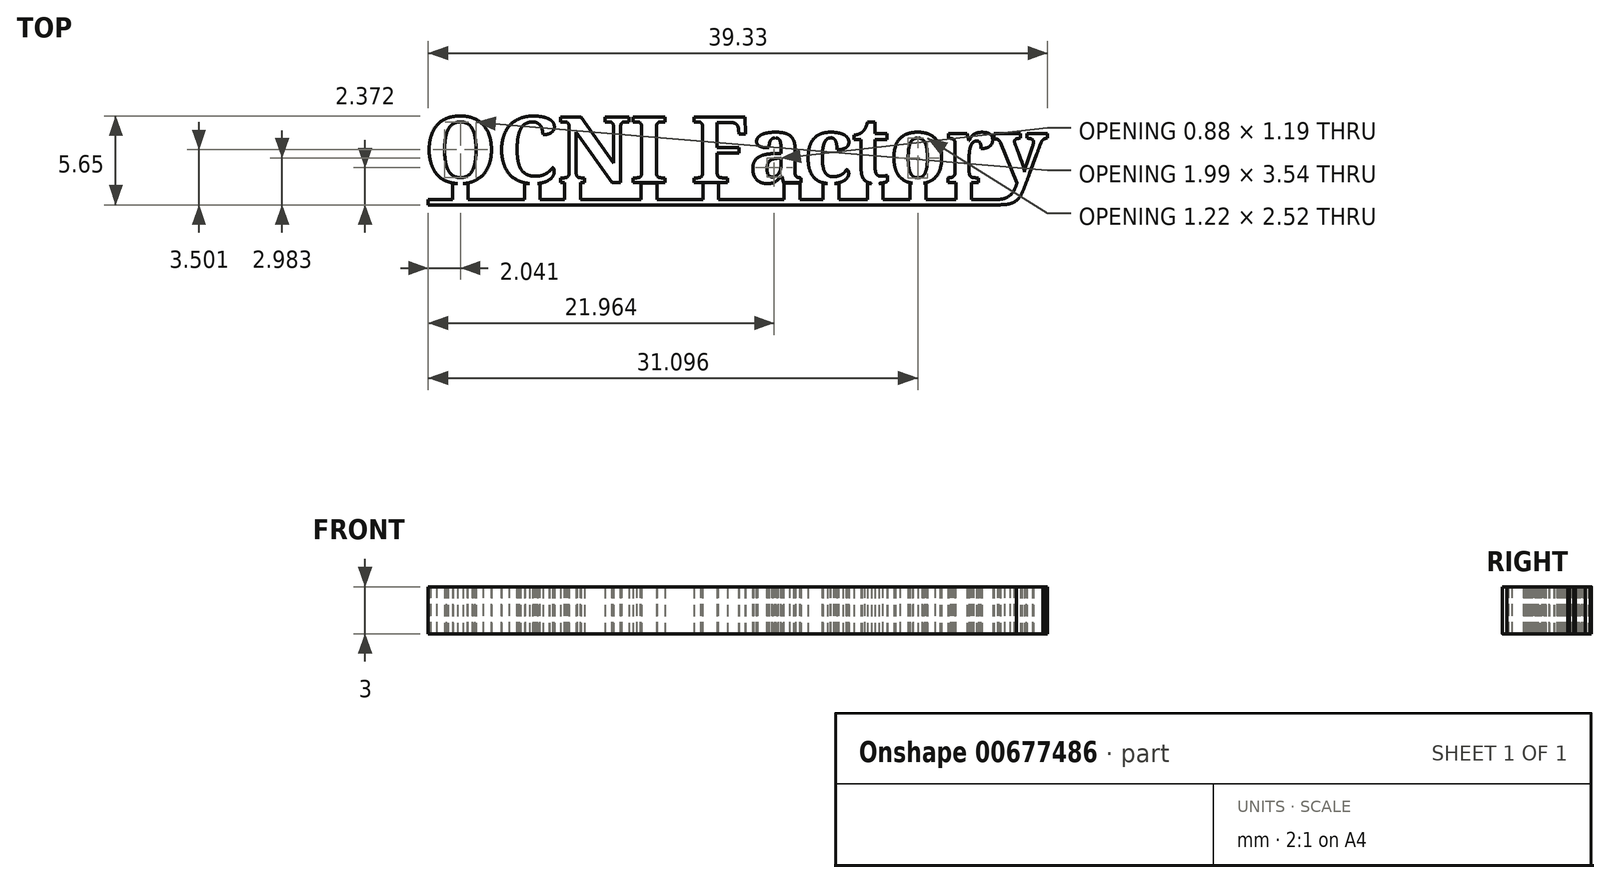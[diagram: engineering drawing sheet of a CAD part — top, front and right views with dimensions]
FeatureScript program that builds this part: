
annotation { "Feature Type Name" : "Feature", "Feature Type Description" : "" }
export const myFeature = defineFeature(function(context is Context, id is Id, definition is map)
    precondition{}
    {
        {
            var Q0;
            Q0=qCreatedBy(makeId("Top.planeOp"),FACE);
            var sketch = newSketch(context, id + "F0", { "sketchPlane" : qUnion([Q0])});
            skText(sketch, "E0", { "text": "OCNI Factory", "fontName": "NotoSerif-Bold.ttf"});
            const initialGuessF0  = {"E0": [-0.00492, -0.00147, 1, 0, 0.00421]};
            skSetInitialGuess(sketch, initialGuessF0);
            skSolve(sketch);
        }
        {
            var Q0;
            Q0 = qSketchRegion(id + "F0", true);
            extrude(context, id + "F1", {"entities" : qUnion([Q0]), "depth" : 3 * mm, "offsetDistance" : 25 * mm});
        }
        {
            var Q0;
            Q0=makeQuery(id+"F1.opExtrude","SWEPT_FACE",FACE,{"disambiguationData":[OSD([sQuery(id+"F0.wireOp",EDGE,"E0.sketch_text.stroke-369")])]});
            var Q1;
            Q1=makeQuery(id+"F1.opExtrude","SWEPT_FACE",FACE,{"disambiguationData":[OSD([sQuery(id+"F0.wireOp",EDGE,"E0.sketch_text.stroke-8")])]});
            extrude(context, id + "F2", {"entities" : qUnion([Q0]), "operationType" : NewBodyOperationType.ADD, "depth" : 36.1 * mm, "endBoundEntityFace" : qUnion([Q1]), "offsetDistance" : 25 * mm});
        }
        {
            var Q0;
            Q0=qCreatedBy(makeId("Top.planeOp"),FACE);
            var sketch = newSketch(context, id + "F3", { "sketchPlane" : qUnion([Q0])});
            skLineSegment(sketch, "E1.bottom", {"start": v(-3.12, -1.52) * mm, "end": v(-2.12, -1.52) * mm});
            skLineSegment(sketch, "E1.top", {"start": v(-3.12, -2.87) * mm, "end": v(-2.12, -2.87) * mm});
            skLineSegment(sketch, "E1.left", {"start": v(-3.12, -1.52) * mm, "end": v(-3.12, -2.87) * mm});
            skLineSegment(sketch, "E1.right", {"start": v(-2.12, -1.52) * mm, "end": v(-2.12, -2.87) * mm});
            skLineSegment(sketch, "E2.bottom", {"start": v(1.46, -1.52) * mm, "end": v(2.46, -1.52) * mm});
            skLineSegment(sketch, "E2.top", {"start": v(1.46, -2.87) * mm, "end": v(2.46, -2.87) * mm});
            skLineSegment(sketch, "E2.left", {"start": v(1.46, -1.52) * mm, "end": v(1.46, -2.87) * mm});
            skLineSegment(sketch, "E2.right", {"start": v(2.46, -1.52) * mm, "end": v(2.46, -2.87) * mm});
            skLineSegment(sketch, "E3.bottom", {"start": v(4, -1.44) * mm, "end": v(5, -1.44) * mm});
            skLineSegment(sketch, "E3.top", {"start": v(4, -2.8) * mm, "end": v(5, -2.8) * mm});
            skLineSegment(sketch, "E3.left", {"start": v(4, -1.44) * mm, "end": v(4, -2.8) * mm});
            skLineSegment(sketch, "E3.right", {"start": v(5, -1.44) * mm, "end": v(5, -2.8) * mm});
            skLineSegment(sketch, "E4.bottom", {"start": v(8.87, -1.47) * mm, "end": v(9.87, -1.47) * mm});
            skLineSegment(sketch, "E4.top", {"start": v(8.87, -2.83) * mm, "end": v(9.87, -2.83) * mm});
            skLineSegment(sketch, "E4.left", {"start": v(8.87, -1.47) * mm, "end": v(8.87, -2.83) * mm});
            skLineSegment(sketch, "E4.right", {"start": v(9.87, -1.47) * mm, "end": v(9.87, -2.83) * mm});
            skLineSegment(sketch, "E5.bottom", {"start": v(12.79, -1.47) * mm, "end": v(13.79, -1.47) * mm});
            skLineSegment(sketch, "E5.top", {"start": v(12.79, -2.85) * mm, "end": v(13.79, -2.85) * mm});
            skLineSegment(sketch, "E5.left", {"start": v(12.79, -1.47) * mm, "end": v(12.79, -2.85) * mm});
            skLineSegment(sketch, "E5.right", {"start": v(13.79, -1.47) * mm, "end": v(13.79, -2.85) * mm});
            skLineSegment(sketch, "E6.bottom", {"start": v(17.95, -1.48) * mm, "end": v(18.95, -1.48) * mm});
            skLineSegment(sketch, "E6.top", {"start": v(17.95, -2.84) * mm, "end": v(18.95, -2.84) * mm});
            skLineSegment(sketch, "E6.left", {"start": v(17.95, -1.48) * mm, "end": v(17.95, -2.84) * mm});
            skLineSegment(sketch, "E6.right", {"start": v(18.95, -1.48) * mm, "end": v(18.95, -2.84) * mm});
            skLineSegment(sketch, "E7.bottom", {"start": v(20.43, -1.52) * mm, "end": v(21.43, -1.52) * mm});
            skLineSegment(sketch, "E7.top", {"start": v(20.43, -2.87) * mm, "end": v(21.43, -2.87) * mm});
            skLineSegment(sketch, "E7.left", {"start": v(20.43, -1.52) * mm, "end": v(20.43, -2.87) * mm});
            skLineSegment(sketch, "E7.right", {"start": v(21.43, -1.52) * mm, "end": v(21.43, -2.87) * mm});
            skLineSegment(sketch, "E8.bottom", {"start": v(23.23, -1.51) * mm, "end": v(24.23, -1.51) * mm});
            skLineSegment(sketch, "E8.top", {"start": v(23.23, -2.87) * mm, "end": v(24.23, -2.87) * mm});
            skLineSegment(sketch, "E8.left", {"start": v(23.23, -1.51) * mm, "end": v(23.23, -2.87) * mm});
            skLineSegment(sketch, "E8.right", {"start": v(24.23, -1.51) * mm, "end": v(24.23, -2.87) * mm});
            skLineSegment(sketch, "E9.bottom", {"start": v(25.94, -1.5) * mm, "end": v(26.94, -1.5) * mm});
            skLineSegment(sketch, "E9.top", {"start": v(25.94, -2.85) * mm, "end": v(26.94, -2.85) * mm});
            skLineSegment(sketch, "E9.left", {"start": v(25.94, -1.5) * mm, "end": v(25.94, -2.85) * mm});
            skLineSegment(sketch, "E9.right", {"start": v(26.94, -1.5) * mm, "end": v(26.94, -2.85) * mm});
            skLineSegment(sketch, "E10.bottom", {"start": v(28.85, -1.46) * mm, "end": v(29.85, -1.46) * mm});
            skLineSegment(sketch, "E10.top", {"start": v(28.85, -2.8) * mm, "end": v(29.85, -2.8) * mm});
            skLineSegment(sketch, "E10.left", {"start": v(28.85, -1.46) * mm, "end": v(28.85, -2.8) * mm});
            skLineSegment(sketch, "E10.right", {"start": v(29.85, -1.46) * mm, "end": v(29.85, -2.8) * mm});
            skSolve(sketch);
        }
        {
            var Q0;
            Q0 = qSketchRegion(id + "F3", true);
            var Q1;
            {var subQ0=sQuery(id+"F0.wireOp",EDGE,"E0.sketch_text.stroke-369");Q1=makeQuery(id+"F2.boolean.opBoolean","MERGE",FACE,{"derivedFrom":[makeQuery(id+"F1.opExtrude","CAP_FACE",FACE,{"disambiguationData":[OSD([sQuery(id+"F0.wireOp",EDGE,"E0.sketch_text.stroke-353"),sQuery(id+"F0.wireOp",EDGE,"E0.sketch_text.stroke-354"),sQuery(id+"F0.wireOp",EDGE,"E0.sketch_text.stroke-355"),sQuery(id+"F0.wireOp",EDGE,"E0.sketch_text.stroke-356"),sQuery(id+"F0.wireOp",EDGE,"E0.sketch_text.stroke-357"),sQuery(id+"F0.wireOp",EDGE,"E0.sketch_text.stroke-358"),sQuery(id+"F0.wireOp",EDGE,"E0.sketch_text.stroke-359"),sQuery(id+"F0.wireOp",EDGE,"E0.sketch_text.stroke-360"),sQuery(id+"F0.wireOp",EDGE,"E0.sketch_text.stroke-361"),sQuery(id+"F0.wireOp",EDGE,"E0.sketch_text.stroke-362"),sQuery(id+"F0.wireOp",EDGE,"E0.sketch_text.stroke-363"),sQuery(id+"F0.wireOp",EDGE,"E0.sketch_text.stroke-364"),sQuery(id+"F0.wireOp",EDGE,"E0.sketch_text.stroke-365"),sQuery(id+"F0.wireOp",EDGE,"E0.sketch_text.stroke-366"),sQuery(id+"F0.wireOp",EDGE,"E0.sketch_text.stroke-367"),sQuery(id+"F0.wireOp",EDGE,"E0.sketch_text.stroke-368"),subQ0,sQuery(id+"F0.wireOp",EDGE,"E0.sketch_text.stroke-370"),sQuery(id+"F0.wireOp",EDGE,"E0.sketch_text.stroke-371"),sQuery(id+"F0.wireOp",EDGE,"E0.sketch_text.stroke-372"),sQuery(id+"F0.wireOp",EDGE,"E0.sketch_text.stroke-373"),sQuery(id+"F0.wireOp",EDGE,"E0.sketch_text.stroke-374"),sQuery(id+"F0.wireOp",EDGE,"E0.sketch_text.stroke-375"),sQuery(id+"F0.wireOp",EDGE,"E0.sketch_text.stroke-376"),sQuery(id+"F0.wireOp",EDGE,"E0.sketch_text.stroke-377"),sQuery(id+"F0.wireOp",EDGE,"E0.sketch_text.stroke-378"),sQuery(id+"F0.wireOp",EDGE,"E0.sketch_text.stroke-379"),sQuery(id+"F0.wireOp",EDGE,"E0.sketch_text.stroke-380"),sQuery(id+"F0.wireOp",EDGE,"E0.sketch_text.stroke-381"),sQuery(id+"F0.wireOp",EDGE,"E0.sketch_text.stroke-382"),sQuery(id+"F0.wireOp",EDGE,"E0.sketch_text.stroke-383"),sQuery(id+"F0.wireOp",EDGE,"E0.sketch_text.stroke-384"),sQuery(id+"F0.wireOp",EDGE,"E0.sketch_text.stroke-385"),sQuery(id+"F0.wireOp",EDGE,"E0.sketch_text.stroke-386"),sQuery(id+"F0.wireOp",EDGE,"E0.sketch_text.stroke-387"),sQuery(id+"F0.wireOp",EDGE,"E0.sketch_text.stroke-388"),sQuery(id+"F0.wireOp",EDGE,"E0.sketch_text.stroke-389"),sQuery(id+"F0.wireOp",EDGE,"E0.sketch_text.stroke-390"),sQuery(id+"F0.wireOp",EDGE,"E0.sketch_text.stroke-391"),sQuery(id+"F0.wireOp",EDGE,"E0.sketch_text.stroke-392"),sQuery(id+"F0.wireOp",EDGE,"E0.sketch_text.stroke-393"),sQuery(id+"F0.wireOp",EDGE,"E0.sketch_text.stroke-394"),sQuery(id+"F0.wireOp",EDGE,"E0.sketch_text.stroke-395"),sQuery(id+"F0.wireOp",EDGE,"E0.sketch_text.stroke-396"),sQuery(id+"F0.wireOp",EDGE,"E0.sketch_text.stroke-397"),sQuery(id+"F0.wireOp",EDGE,"E0.sketch_text.stroke-398"),sQuery(id+"F0.wireOp",EDGE,"E0.sketch_text.stroke-399"),sQuery(id+"F0.wireOp",EDGE,"E0.sketch_text.stroke-400"),sQuery(id+"F0.wireOp",EDGE,"E0.sketch_text.stroke-401"),sQuery(id+"F0.wireOp",EDGE,"E0.sketch_text.stroke-402"),sQuery(id+"F0.wireOp",EDGE,"E0.sketch_text.stroke-403"),sQuery(id+"F0.wireOp",EDGE,"E0.sketch_text.stroke-404"),sQuery(id+"F0.wireOp",EDGE,"E0.sketch_text.stroke-405"),sQuery(id+"F0.wireOp",EDGE,"E0.sketch_text.stroke-406")])],"isStart":false}),makeQuery(id+"F2.opExtrude","SWEPT_FACE",FACE,{"disambiguationData":[OSD([subQ0]),TDD([makeQuery(id+"F1.opExtrude","CAP_EDGE",EDGE,{"disambiguationData":[OSD([subQ0])],"isStart":false})])]})]});}
            extrude(context, id + "F4", {"entities" : qUnion([Q0]), "operationType" : NewBodyOperationType.ADD, "endBound" : BoundingType.UP_TO_SURFACE, "depth" : 25 * mm, "endBoundEntityFace" : qUnion([Q1]), "offsetDistance" : 25 * mm});
        }
    });
